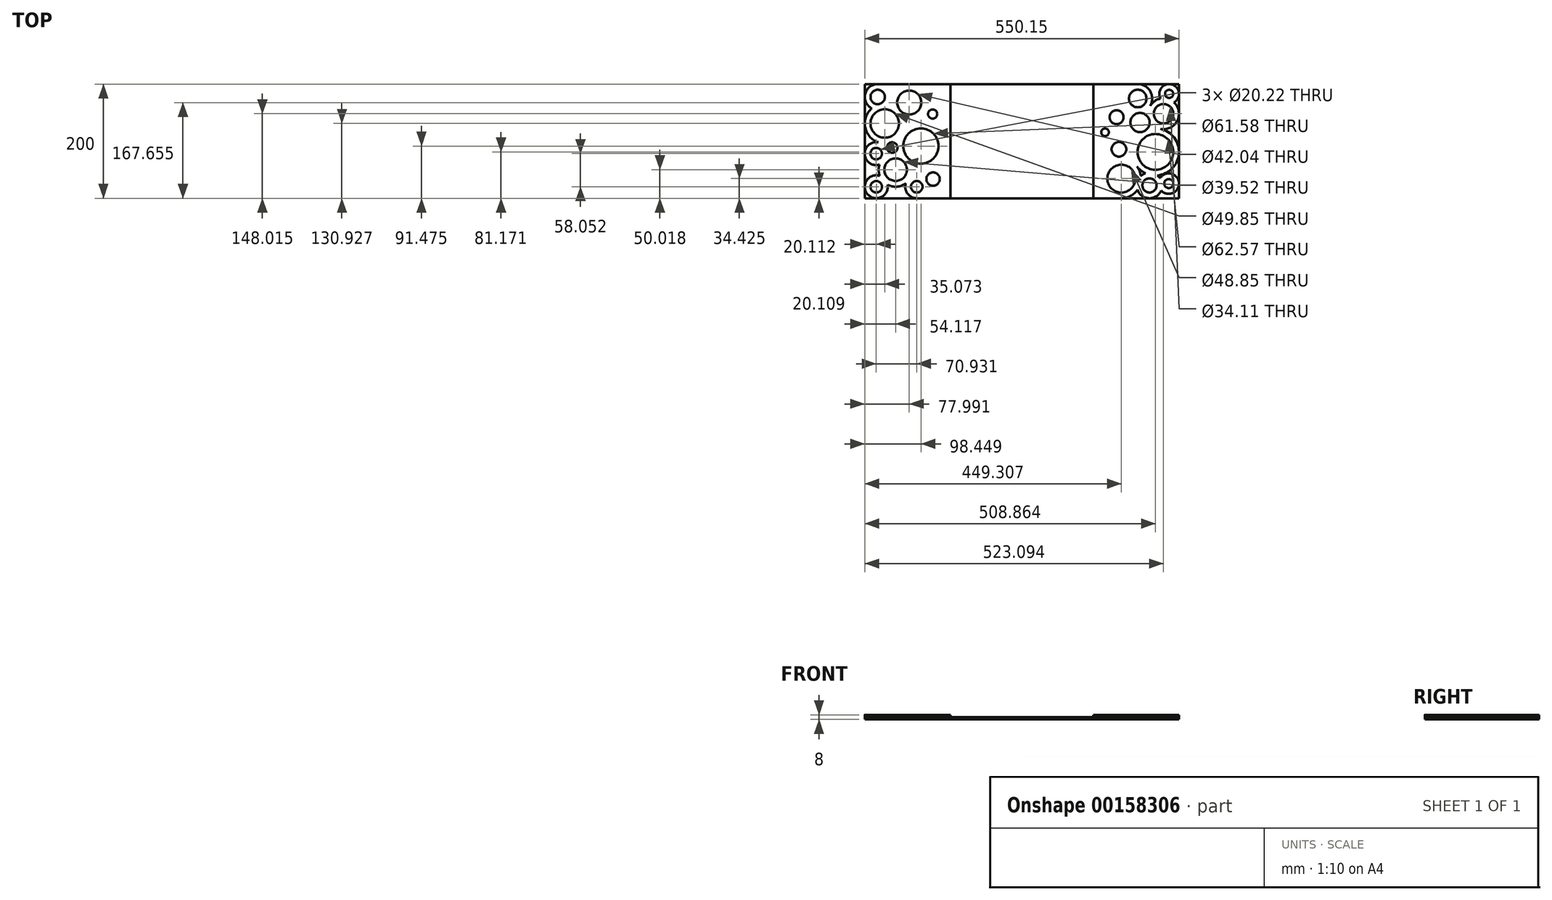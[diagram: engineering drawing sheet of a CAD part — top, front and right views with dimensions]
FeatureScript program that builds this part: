
annotation { "Feature Type Name" : "Feature", "Feature Type Description" : "" }
export const myFeature = defineFeature(function(context is Context, id is Id, definition is map)
    precondition{}
    {
        {
            assignVariable(context, id + "F0", {"name" : "depth", "anyValue" : 4});
        }
        {
            var Q0;
            Q0=qCreatedBy(makeId("Top.planeOp"),FACE);
            var sketch = newSketch(context, id + "F1", { "sketchPlane" : qUnion([Q0])});
            skLineSegment(sketch, "E0.bottom", {"start": v(-125, 100) * mm, "end": v(125, 100) * mm});
            skLineSegment(sketch, "E0.top", {"start": v(-125, -100) * mm, "end": v(125, -100) * mm});
            skLineSegment(sketch, "E0.left", {"start": v(-125, 100) * mm, "end": v(-125, -100) * mm});
            skLineSegment(sketch, "E0.right", {"start": v(125, 100) * mm, "end": v(125, -100) * mm});
            skPoint(sketch, "E0.middle", {"position": v(0, 0) * mm});
            skSolve(sketch);
        }
        {
            var Q0;
            Q0 = qSketchRegion(id + "F1", true);
            extrude(context, id + "F2", {"entities" : qUnion([Q0]), "depth" : (getVariable(context, 'depth')) * mm});
        }
        {
            var Q0;
            Q0=makeQuery(id+"F2.opExtrude","CAP_FACE",FACE,{"disambiguationData":[OSD([sQuery(id+"F1.wireOp",EDGE,"E0.bottom"),sQuery(id+"F1.wireOp",EDGE,"E0.top"),sQuery(id+"F1.wireOp",EDGE,"E0.left"),sQuery(id+"F1.wireOp",EDGE,"E0.right")])],"isStart":false});
            var sketch = newSketch(context, id + "F3", { "sketchPlane" : qUnion([Q0])});
            skLineSegment(sketch, "E1.bottom", {"start": v(-125, -100) * mm, "end": v(-275, -100) * mm});
            skLineSegment(sketch, "E1.top", {"start": v(-125, 100) * mm, "end": v(-275, 100) * mm});
            skLineSegment(sketch, "E1.left", {"start": v(-125, -100) * mm, "end": v(-125, 100) * mm});
            skLineSegment(sketch, "E1.right", {"start": v(-275, -100) * mm, "end": v(-275, 100) * mm});
            skLineSegment(sketch, "E2.bottom", {"start": v(125, 100) * mm, "end": v(275, 100) * mm});
            skLineSegment(sketch, "E2.top", {"start": v(125, -100) * mm, "end": v(275, -100) * mm});
            skLineSegment(sketch, "E2.left", {"start": v(125, 100) * mm, "end": v(125, -100) * mm});
            skLineSegment(sketch, "E2.right", {"start": v(275, 100) * mm, "end": v(275, -100) * mm});
            skSolve(sketch);
        }
        {
            var Q0;
            Q0 = qSketchRegion(id + "F3", true);
            extrude(context, id + "F4", {"entities" : qUnion([Q0]), "oppositeDirection" : true, "depth" : (getVariable(context, 'depth')) * mm});
        }
        {
            var Q0;
            Q0=makeQuery(id+"F4.opExtrude","CAP_FACE",FACE,{"disambiguationData":[OSD([sQuery(id+"F3.wireOp",EDGE,"E1.bottom"),sQuery(id+"F3.wireOp",EDGE,"E1.top"),sQuery(id+"F3.wireOp",EDGE,"E1.left"),sQuery(id+"F3.wireOp",EDGE,"E1.right")])],"isStart":true});
            var sketch = newSketch(context, id + "F5", { "sketchPlane" : qUnion([Q0])});
            skCircle(sketch, "E3", {"center": v(-252.4, 77.4) * mm, "radius": 12.6 * mm});
            skCircle(sketch, "E4", {"center": v(-252.4, 77.4) * mm, "radius": 22.6 * mm});
            skCircle(sketch, "E5", {"center": v(-240.08, 30.93) * mm, "radius": 24.92 * mm});
            skCircle(sketch, "E6", {"center": v(-240.08, 30.93) * mm, "radius": 34.92 * mm});
            skCircle(sketch, "E7", {"center": v(-254.9, -79.9) * mm, "radius": 10.1 * mm});
            skCircle(sketch, "E8", {"center": v(-254.9, -79.9) * mm, "radius": 20.1 * mm});
            skCircle(sketch, "E9", {"center": v(-221.03, -49.98) * mm, "radius": 19.76 * mm});
            skCircle(sketch, "E10", {"center": v(-221.03, -49.98) * mm, "radius": 29.76 * mm});
            skCircle(sketch, "E11", {"center": v(-255.04, -21.84) * mm, "radius": 10.1 * mm});
            skCircle(sketch, "E12", {"center": v(-255.04, -21.84) * mm, "radius": 20.1 * mm});
            skCircle(sketch, "E13", {"center": v(-227.02, -11.2) * mm, "radius": 9.2 * mm});
            skLineSegment(sketch, "E14", {"start": v(-125, 100) * mm, "end": v(-125, -100) * mm});
            skLineSegment(sketch, "E15", {"start": v(-252.4, 100) * mm, "end": v(-125, 100) * mm});
            skCircle(sketch, "E16", {"center": v(-184.1, -79.9) * mm, "radius": 10.1 * mm});
            skCircle(sketch, "E17", {"center": v(-184.1, -79.9) * mm, "radius": 20.1 * mm});
            skCircle(sketch, "E18", {"center": v(-197.16, 67.65) * mm, "radius": 21.02 * mm});
            skCircle(sketch, "E19", {"center": v(-156.24, 47.47) * mm, "radius": 8.05 * mm});
            skCircle(sketch, "E20", {"center": v(-176.7, -8.53) * mm, "radius": 30.8 * mm});
            skLineSegment(sketch, "E21", {"start": v(-184.1, -100) * mm, "end": v(-125, -100) * mm});
            skCircle(sketch, "E22", {"center": v(-155.43, -66.4) * mm, "radius": 11.7 * mm});
            skSolve(sketch);
        }
        {
            var Q0;
            Q0 = qSketchRegion(id + "F5", true);
            extrude(context, id + "F6", {"entities" : qUnion([Q0]), "depth" : (getVariable(context, 'depth')) * mm});
        }
        {
            var Q0;
            Q0=makeQuery(id+"F4.opExtrude","CAP_FACE",FACE,{"disambiguationData":[OSD([sQuery(id+"F3.wireOp",EDGE,"E2.bottom"),sQuery(id+"F3.wireOp",EDGE,"E2.top"),sQuery(id+"F3.wireOp",EDGE,"E2.left"),sQuery(id+"F3.wireOp",EDGE,"E2.right")])],"isStart":true});
            var sketch = newSketch(context, id + "F7", { "sketchPlane" : qUnion([Q0])});
            skLineSegment(sketch, "E23", {"start": v(125, 100) * mm, "end": v(125, -100) * mm});
            skCircle(sketch, "E24", {"center": v(257.8, 82.8) * mm, "radius": 7.2 * mm});
            skCircle(sketch, "E25", {"center": v(233.71, -18.83) * mm, "radius": 31.29 * mm});
            skCircle(sketch, "E26", {"center": v(233.71, -18.83) * mm, "radius": 41.29 * mm});
            skCircle(sketch, "E27", {"center": v(247.94, 48.01) * mm, "radius": 17.06 * mm});
            skCircle(sketch, "E28", {"center": v(247.94, 48.01) * mm, "radius": 27.06 * mm});
            skCircle(sketch, "E29", {"center": v(174.16, -65.58) * mm, "radius": 24.42 * mm});
            skCircle(sketch, "E30", {"center": v(174.16, -65.58) * mm, "radius": 34.42 * mm});
            skCircle(sketch, "E31", {"center": v(206.82, 32.7) * mm, "radius": 16.83 * mm});
            skCircle(sketch, "E32", {"center": v(202.84, 74.67) * mm, "radius": 15.33 * mm});
            skCircle(sketch, "E33", {"center": v(202.84, 74.67) * mm, "radius": 25.33 * mm});
            skCircle(sketch, "E34", {"center": v(165.77, 41.89) * mm, "radius": 12.22 * mm});
            skCircle(sketch, "E35", {"center": v(145.6, 15.55) * mm, "radius": 6.66 * mm});
            skLineSegment(sketch, "E36", {"start": v(125, 100) * mm, "end": v(202.84, 100) * mm});
            skLineSegment(sketch, "E37", {"start": v(174.16, -100) * mm, "end": v(125, -100) * mm});
            skCircle(sketch, "E38", {"center": v(169.94, -14.29) * mm, "radius": 12.87 * mm});
            skCircle(sketch, "E39", {"center": v(257.8, 82.8) * mm, "radius": 17.2 * mm});
            skCircle(sketch, "E40", {"center": v(223.37, -77.59) * mm, "radius": 12.41 * mm});
            skCircle(sketch, "E41", {"center": v(223.37, -77.59) * mm, "radius": 22.41 * mm});
            skCircle(sketch, "E42", {"center": v(257.1, -74.36) * mm, "radius": 7.9 * mm});
            skCircle(sketch, "E43", {"center": v(257.1, -74.36) * mm, "radius": 17.9 * mm});
            skSolve(sketch);
        }
        {
            var Q0;
            Q0 = qSketchRegion(id + "F7", true);
            extrude(context, id + "F8", {"entities" : qUnion([Q0]), "depth" : (getVariable(context, 'depth')) * mm});
        }
    });
